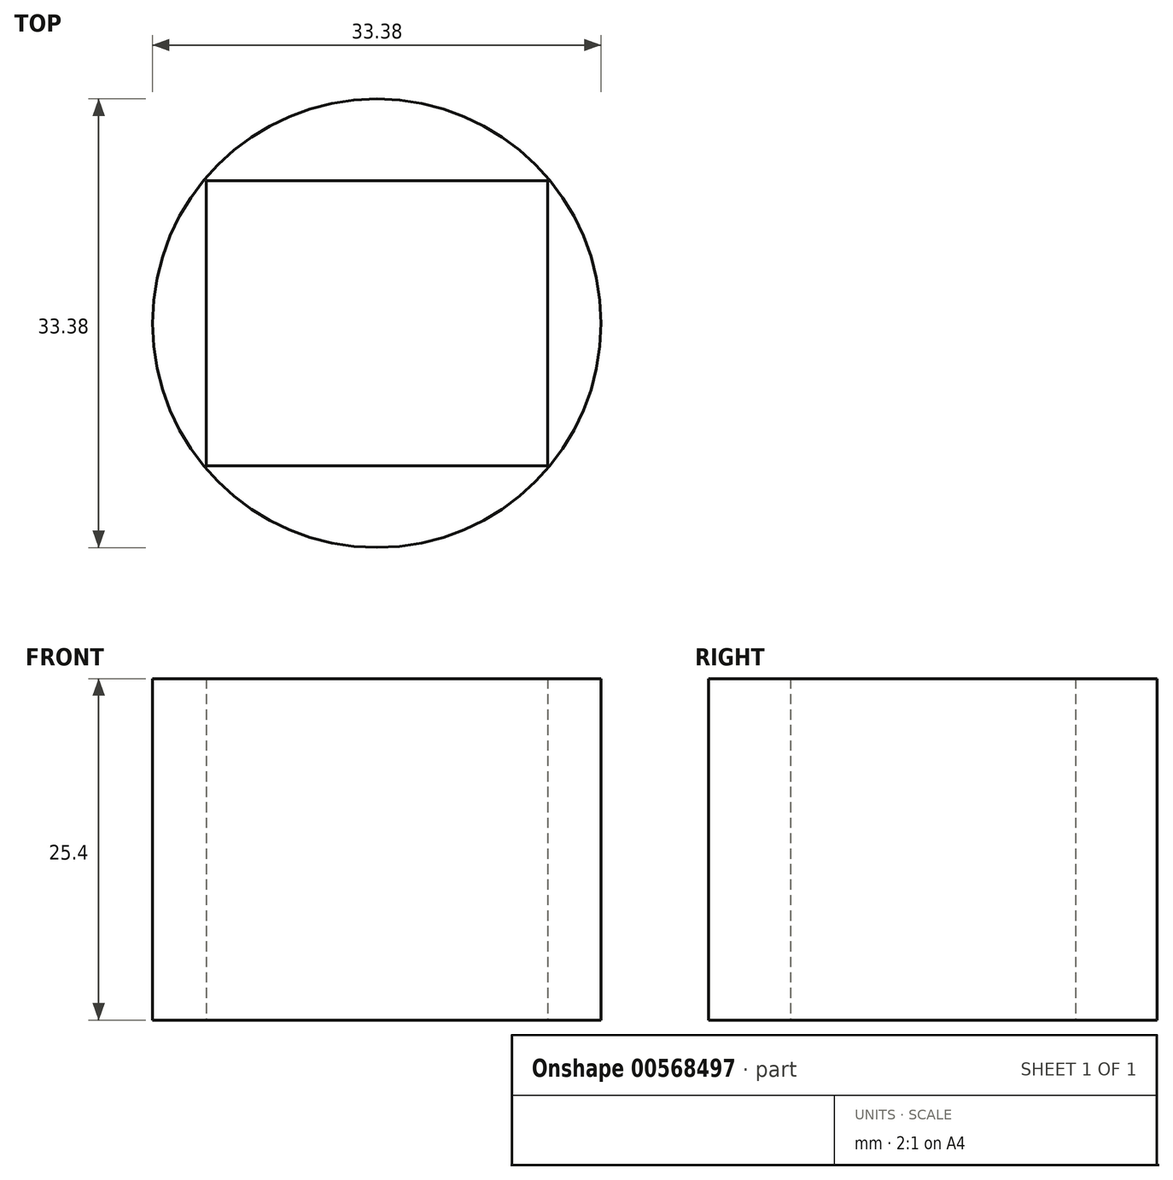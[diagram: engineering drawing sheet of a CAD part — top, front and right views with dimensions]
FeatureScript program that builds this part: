
annotation { "Feature Type Name" : "Feature", "Feature Type Description" : "" }
export const myFeature = defineFeature(function(context is Context, id is Id, definition is map)
    precondition{}
    {
        {
            var Q0;
            Q0=qCreatedBy(makeId("Top.planeOp"),FACE);
            var sketch = newSketch(context, id + "F0", { "sketchPlane" : qUnion([Q0])});
            skCircle(sketch, "E0", {"center": v(0, 0) * mm, "radius": 16.69 * mm});
            skLineSegment(sketch, "E1.bottom", {"start": v(-12.7, 10.6) * mm, "end": v(12.7, 10.6) * mm});
            skLineSegment(sketch, "E1.top", {"start": v(-12.7, -10.6) * mm, "end": v(12.7, -10.6) * mm});
            skLineSegment(sketch, "E1.left", {"start": v(-12.7, 10.6) * mm, "end": v(-12.7, -10.6) * mm});
            skLineSegment(sketch, "E1.right", {"start": v(12.7, 10.6) * mm, "end": v(12.7, -10.6) * mm});
            skPoint(sketch, "E2", {"position": v(0, 16.69) * mm});
            skPoint(sketch, "E3", {"position": v(16.69, 0) * mm});
            skPoint(sketch, "E3.positionSnap0", {"position": v(12.7, 0) * mm});
            skSolve(sketch);
        }
        {
            var Q0;
            Q0 = qSketchRegion(id + "F0", true);
            extrude(context, id + "F1", {"entities" : qUnion([Q0]), "depth" : 25.4 * mm, "offsetDistance" : 25.4 * mm});
        }
    });
